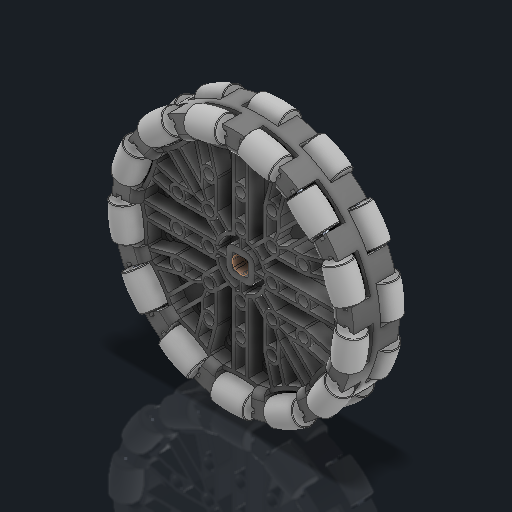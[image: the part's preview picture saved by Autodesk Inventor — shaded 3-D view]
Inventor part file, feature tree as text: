
AUTODESK INVENTOR PART (.ipt)
format: ipt  version: 2023.2 (Build 272271030, 271C)  size: 4,552,192 bytes
history: native  units: in
note: dims shown in document units (in); Inventor stores cm internally (conversion verified against a paired STEP export)
features: other x57, sketch x1
ambient origin geometry x8: Origin, YZ Plane, XZ Plane, XY Plane, X Axis, Y Axis, Z Axis, Center Point
bodies: Solid1 (feature_tree), Solid2 (feature_tree), Solid3 (feature_tree), Solid4 (feature_tree), Solid5 (feature_tree), Solid6 (feature_tree), Solid7 (feature_tree), Solid8 (feature_tree), Solid9 (feature_tree), Solid10 (feature_tree), Solid11 (feature_tree), Solid12 (feature_tree), Solid13 (feature_tree), Solid14 (feature_tree), Solid15 (feature_tree), Solid16 (feature_tree), Solid17 (feature_tree), Solid18 (feature_tree), Solid19 (feature_tree), Solid20 (feature_tree), Solid21 (feature_tree), Solid22 (feature_tree), Solid23 (feature_tree), Solid24 (feature_tree), Solid25 (feature_tree), Solid26 (feature_tree), Solid27 (feature_tree), Solid28 (feature_tree), Solid29 (feature_tree), Solid30 (feature_tree), Solid31 (feature_tree), Solid32 (feature_tree), Solid33 (feature_tree), Solid34 (feature_tree), Solid35 (feature_tree), Solid36 (feature_tree), Solid37 (feature_tree), Solid38 (feature_tree), Solid39 (feature_tree), Solid40 (feature_tree), Solid41 (feature_tree), Solid42 (feature_tree), Solid43 (feature_tree), Solid44 (feature_tree), Solid45 (feature_tree), Solid46 (feature_tree), Solid47 (feature_tree), Solid48 (feature_tree), Solid49 (feature_tree), Solid50 (feature_tree), Solid51 (feature_tree), Solid52 (feature_tree), Solid53 (feature_tree)
feature tree (58):
  other  "4 Omni Antistatic.ipt"
  other  "Solid1::4 Omni Antistatic.ipt"
  other  "Solid2::4 Omni Antistatic.ipt"
  other  "Solid3::4 Omni Antistatic.ipt"
  other  "Solid4::4 Omni Antistatic.ipt"
  other  "Solid5::4 Omni Antistatic.ipt"
  other  "Solid6::4 Omni Antistatic.ipt"
  other  "Solid7::4 Omni Antistatic.ipt"
  other  "Solid8::4 Omni Antistatic.ipt"
  other  "Solid9::4 Omni Antistatic.ipt"
  other  "Solid10::4 Omni Antistatic.ipt"
  other  "Solid11::4 Omni Antistatic.ipt"
  other  "Solid12::4 Omni Antistatic.ipt"
  other  "Solid13::4 Omni Antistatic.ipt"
  other  "Solid14::4 Omni Antistatic.ipt"
  other  "Solid15::4 Omni Antistatic.ipt"
  other  "Solid16::4 Omni Antistatic.ipt"
  other  "Solid17::4 Omni Antistatic.ipt"
  other  "Solid18::4 Omni Antistatic.ipt"
  other  "Solid19::4 Omni Antistatic.ipt"
  other  "Solid20::4 Omni Antistatic.ipt"
  other  "Solid21::4 Omni Antistatic.ipt"
  other  "Solid22::4 Omni Antistatic.ipt"
  other  "Solid23::4 Omni Antistatic.ipt"
  other  "Solid24::4 Omni Antistatic.ipt"
  other  "Solid25::4 Omni Antistatic.ipt"
  other  "Solid26::4 Omni Antistatic.ipt"
  other  "Solid27::4 Omni Antistatic.ipt"
  other  "Solid28::4 Omni Antistatic.ipt"
  other  "Solid29::4 Omni Antistatic.ipt"
  other  "Solid30::4 Omni Antistatic.ipt"
  other  "Solid31::4 Omni Antistatic.ipt"
  other  "Solid32::4 Omni Antistatic.ipt"
  other  "Solid33::4 Omni Antistatic.ipt"
  other  "Solid34::4 Omni Antistatic.ipt"
  other  "Solid35::4 Omni Antistatic.ipt"
  other  "Solid36::4 Omni Antistatic.ipt"
  other  "Solid37::4 Omni Antistatic.ipt"
  other  "Solid38::4 Omni Antistatic.ipt"
  other  "Solid39::4 Omni Antistatic.ipt"
  other  "Solid40::4 Omni Antistatic.ipt"
  other  "Solid41::4 Omni Antistatic.ipt"
  other  "Solid42::4 Omni Antistatic.ipt"
  other  "Solid43::4 Omni Antistatic.ipt"
  other  "Solid44::4 Omni Antistatic.ipt"
  other  "Solid45::4 Omni Antistatic.ipt"
  other  "Solid46::4 Omni Antistatic.ipt"
  other  "Solid47::4 Omni Antistatic.ipt"
  other  "Solid48::4 Omni Antistatic.ipt"
  other  "Solid49::4 Omni Antistatic.ipt"
  other  "Solid50::4 Omni Antistatic.ipt"
  other  "Solid51::4 Omni Antistatic.ipt"
  other  "Solid52::4 Omni Antistatic.ipt"
  other  "Solid53::4 Omni Antistatic.ipt"
  other  "TaggingFeature1"
  sketch  "Sketch1"  dims[d0=0.3937in]
  other  "Srf1"
  other  "Srf1::Derived"
